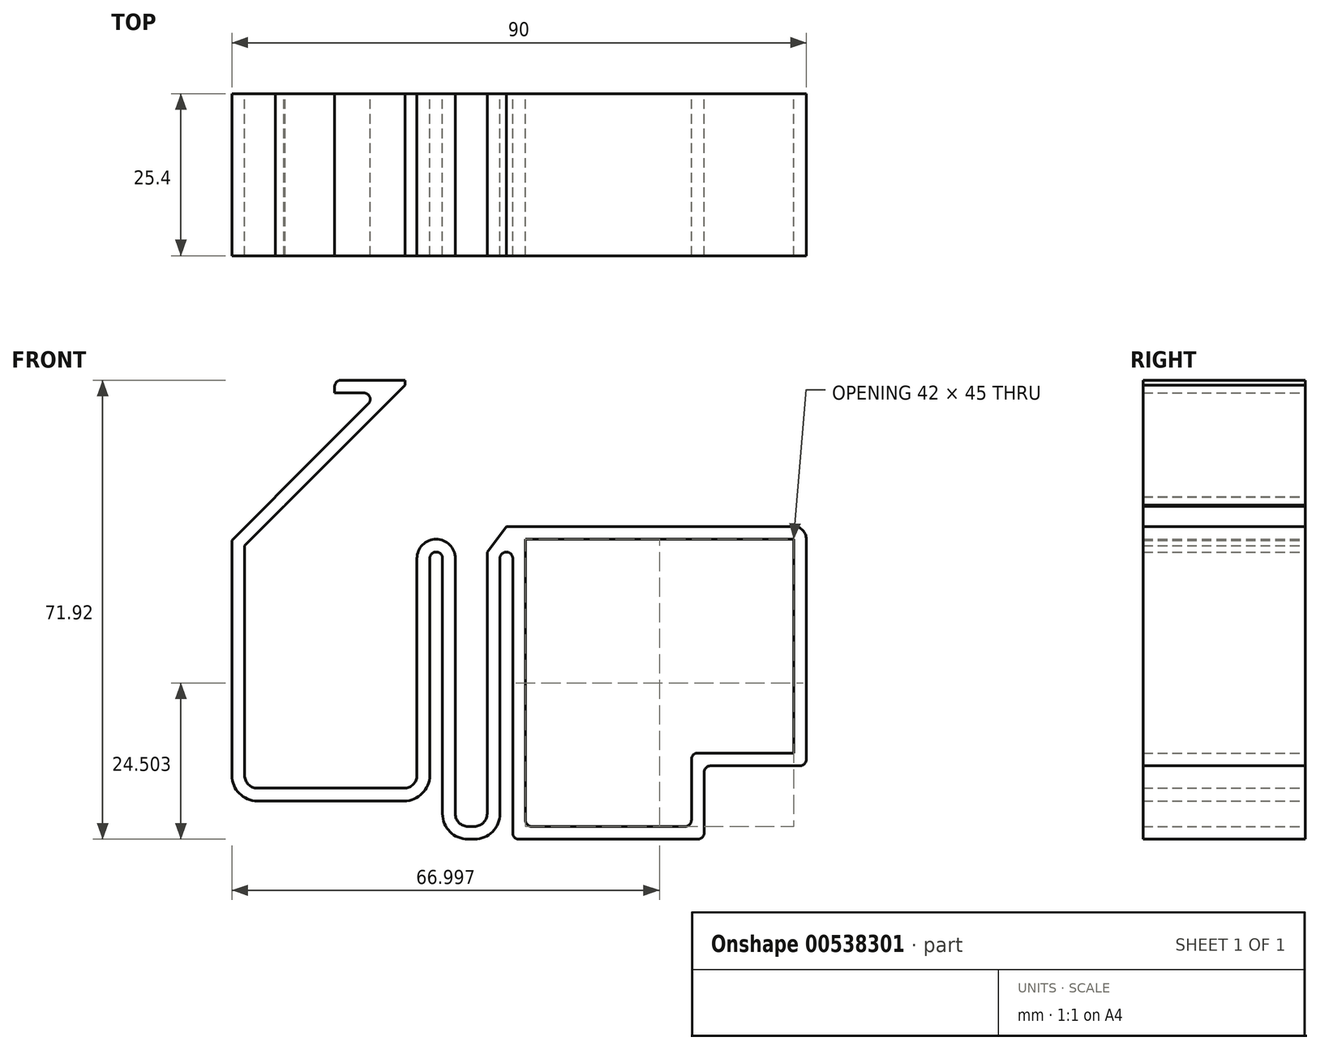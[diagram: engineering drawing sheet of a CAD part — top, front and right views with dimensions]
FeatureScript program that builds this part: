
annotation { "Feature Type Name" : "Feature", "Feature Type Description" : "" }
export const myFeature = defineFeature(function(context is Context, id is Id, definition is map)
    precondition{}
    {
        {
            var Q0;
            Q0=qCreatedBy(makeId("Front.planeOp"),FACE);
            var sketch = newSketch(context, id + "F0", { "sketchPlane" : qUnion([Q0])});
            skLineSegment(sketch, "E0", {"start": v(-44.1, 16.34) * mm, "end": v(-44.1, -17.66) * mm});
            skLineSegment(sketch, "E1", {"start": v(-17.1, -17.66) * mm, "end": v(-17.1, 16.34) * mm});
            skLineSegment(sketch, "E2", {"start": v(-0.1, 16.34) * mm, "end": v(-0.1, -24.66) * mm});
            skLineSegment(sketch, "E3", {"start": v(-11.1, -23.66) * mm, "end": v(-11.1, 16.34) * mm});
            skLineSegment(sketch, "E4", {"start": v(-6.1, -23.66) * mm, "end": v(-6.1, 16.34) * mm});
            skLineSegment(sketch, "E5", {"start": v(-9.1, -25.66) * mm, "end": v(-8.1, -25.66) * mm});
            skArc(sketch, "E6", {"start": v(-11.1, 16.34) * mm, "mid": v(-14.1, 19.34) * mm, "end": v(-17.1, 16.34) * mm});
            skPoint(sketch, "E7.visualSharp", {"position": v(-11.1, -25.66) * mm});
            skArc(sketch, "E7.filletArc", {"start": v(-11.1, -23.66) * mm, "mid": v(-10.5, -25.07) * mm, "end": v(-9.1, -25.66) * mm});
            skPoint(sketch, "E8.visualSharp", {"position": v(-6.1, -25.66) * mm});
            skArc(sketch, "E8.filletArc", {"start": v(-8.1, -25.66) * mm, "mid": v(-6.68, -25.07) * mm, "end": v(-6.1, -23.66) * mm});
            skPoint(sketch, "E9.visualSharp", {"position": v(5.9, -15.66) * mm});
            skPoint(sketch, "E10.visualSharp", {"position": v(-17.1, -25.66) * mm});
            skPoint(sketch, "E11.visualSharp", {"position": v(-44.1, -25.66) * mm});
            skPoint(sketch, "E12.end.orphan", {"position": v(20.34, -15.66) * mm});
            skLineSegment(sketch, "E13", {"start": v(20.34, -15.66) * mm, "end": v(20.9, -15.66) * mm});
            skPoint(sketch, "E14.endSnap0", {"position": v(-3.1, 19.34) * mm});
            skLineSegment(sketch, "E15", {"start": v(-42.1, -19.66) * mm, "end": v(-19.1, -19.66) * mm});
            skPoint(sketch, "E16.visualSharp", {"position": v(-44.1, -19.66) * mm});
            skArc(sketch, "E16.filletArc", {"start": v(-44.1, -17.66) * mm, "mid": v(-43.5, -19.07) * mm, "end": v(-42.1, -19.66) * mm});
            skPoint(sketch, "E17.visualSharp", {"position": v(-17.1, -19.66) * mm});
            skArc(sketch, "E17.filletArc", {"start": v(-19.1, -19.66) * mm, "mid": v(-17.68, -19.07) * mm, "end": v(-17.1, -17.66) * mm});
            skLineSegment(sketch, "E18.0", {"start": v(-2.1, 16.34) * mm, "end": v(-2.1, -25.66) * mm});
            skLineSegment(sketch, "E19.0", {"start": v(-4.1, -23.66) * mm, "end": v(-4.1, 16.34) * mm});
            skLineSegment(sketch, "E19.1", {"start": v(-13.1, -23.66) * mm, "end": v(-13.1, 16.34) * mm});
            skArc(sketch, "E19.2", {"start": v(-13.1, -23.66) * mm, "mid": v(-11.92, -26.49) * mm, "end": v(-9.1, -27.66) * mm});
            skLineSegment(sketch, "E19.3", {"start": v(-9.1, -27.66) * mm, "end": v(-8.1, -27.66) * mm});
            skArc(sketch, "E19.4", {"start": v(-8.1, -27.66) * mm, "mid": v(-5.26, -26.49) * mm, "end": v(-4.1, -23.66) * mm});
            skArc(sketch, "E20", {"start": v(-2.1, 16.34) * mm, "mid": v(-3.1, 17.34) * mm, "end": v(-4.1, 16.34) * mm});
            skLineSegment(sketch, "E21.0", {"start": v(-15.1, -17.66) * mm, "end": v(-15.1, 16.34) * mm});
            skLineSegment(sketch, "E21.1", {"start": v(-46.1, 16.34) * mm, "end": v(-46.1, -17.66) * mm});
            skArc(sketch, "E21.2", {"start": v(-46.1, -17.66) * mm, "mid": v(-44.92, -20.49) * mm, "end": v(-42.1, -21.66) * mm});
            skLineSegment(sketch, "E21.3", {"start": v(-42.1, -21.66) * mm, "end": v(-19.1, -21.66) * mm});
            skArc(sketch, "E21.4", {"start": v(-19.1, -21.66) * mm, "mid": v(-16.26, -20.49) * mm, "end": v(-15.1, -17.66) * mm});
            skArc(sketch, "E22", {"start": v(-13.1, 16.34) * mm, "mid": v(-14.1, 17.34) * mm, "end": v(-15.1, 16.34) * mm});
            skPoint(sketch, "E23.visualSharp", {"position": v(22.9, -15.66) * mm});
            skPoint(sketch, "E24.visualSharp", {"position": v(24.9, -17.66) * mm});
            skLineSegment(sketch, "E25", {"start": v(-9.1, -25.66) * mm, "end": v(-8.1, -25.66) * mm, "construction": true});
            skLineSegment(sketch, "E26", {"start": v(-1.1, -27.66) * mm, "end": v(26.9, -27.66) * mm, "construction": true});
            skLineSegment(sketch, "E27", {"start": v(0.9, -25.66) * mm, "end": v(24.9, -25.66) * mm});
            skPoint(sketch, "E27.endSnap0", {"position": v(15.4, -25.66) * mm});
            skLineSegment(sketch, "E28", {"start": v(-2.1, -25.66) * mm, "end": v(-2.1, -26.66) * mm});
            skLineSegment(sketch, "E29", {"start": v(-2.1, -27.66) * mm, "end": v(27.9, -27.66) * mm});
            skLineSegment(sketch, "E30.trimOffspring", {"start": v(2.9, -25.66) * mm, "end": v(24.9, -25.66) * mm, "construction": true});
            skPoint(sketch, "E31.center.orphan", {"position": v(2.9, -25.66) * mm});
            skPoint(sketch, "E32.start.orphan", {"position": v(5.9, -25.66) * mm});
            skPoint(sketch, "E33.end.orphan", {"position": v(22.9, 19.34) * mm});
            skPoint(sketch, "E34.orphan", {"position": v(-2.1, -36.17) * mm});
            skLineSegment(sketch, "E35", {"start": v(25.9, -15.16) * mm, "end": v(25.9, -24.66) * mm});
            skPoint(sketch, "E36.orphan", {"position": v(39.89, -25.66) * mm});
            skLineSegment(sketch, "E37.0", {"start": v(27.9, -17.16) * mm, "end": v(27.9, -25.66) * mm});
            skLineSegment(sketch, "E38.trimOffspring", {"start": v(39.89, -25.66) * mm, "end": v(45.22, -25.66) * mm});
            skLineSegment(sketch, "E39", {"start": v(27.9, -25.66) * mm, "end": v(27.9, -26.66) * mm});
            skPoint(sketch, "E40.visualSharp", {"position": v(-0.1, -25.66) * mm});
            skArc(sketch, "E40.filletArc", {"start": v(-0.1, -24.66) * mm, "mid": v(0.2, -25.36) * mm, "end": v(0.9, -25.66) * mm});
            skPoint(sketch, "E41.visualSharp", {"position": v(25.9, -25.66) * mm});
            skArc(sketch, "E41.filletArc", {"start": v(24.9, -25.66) * mm, "mid": v(25.61, -25.36) * mm, "end": v(25.9, -24.66) * mm});
            skPoint(sketch, "E42.visualSharp", {"position": v(27.9, -27.66) * mm});
            skArc(sketch, "E42.filletArc", {"start": v(26.9, -27.66) * mm, "mid": v(27.61, -27.36) * mm, "end": v(27.9, -26.66) * mm});
            skPoint(sketch, "E43.visualSharp", {"position": v(-2.1, -27.66) * mm});
            skArc(sketch, "E43.filletArc", {"start": v(-2.1, -26.66) * mm, "mid": v(-1.8, -27.36) * mm, "end": v(-1.1, -27.66) * mm});
            skPoint(sketch, "E44.visualSharp", {"position": v(25.9, -14.16) * mm});
            skArc(sketch, "E44.filletArc", {"start": v(26.9, -14.16) * mm, "mid": v(26.2, -14.45) * mm, "end": v(25.9, -15.16) * mm});
            skPoint(sketch, "E45.visualSharp", {"position": v(27.9, -16.16) * mm});
            skArc(sketch, "E45.filletArc", {"start": v(28.9, -16.16) * mm, "mid": v(28.2, -16.45) * mm, "end": v(27.9, -17.16) * mm});
            skLineSegment(sketch, "E46", {"start": v(41.9, -8.41) * mm, "end": v(41.9, -14.16) * mm});
            skLineSegment(sketch, "E47", {"start": v(36.16, -19.88) * mm, "end": v(36.37, -19.88) * mm});
            skLineSegment(sketch, "E48", {"start": v(26.9, -14.16) * mm, "end": v(41.9, -14.16) * mm});
            skLineSegment(sketch, "E49", {"start": v(41.9, -14.16) * mm, "end": v(41.9, 15.92) * mm});
            skLineSegment(sketch, "E50.0", {"start": v(43.9, -14.16) * mm, "end": v(43.9, 15.92) * mm});
            skLineSegment(sketch, "E51", {"start": v(43.9, -14.16) * mm, "end": v(43.9, -15.14) * mm});
            skLineSegment(sketch, "E52.trimOffspring", {"start": v(28.9, -16.16) * mm, "end": v(42.9, -16.16) * mm});
            skPoint(sketch, "E53.endSnap0", {"position": v(-3.1, 17.34) * mm});
            skPoint(sketch, "E54.orphan", {"position": v(43.83, 17.34) * mm});
            skPoint(sketch, "E55.visualSharp", {"position": v(43.06, 19.34) * mm});
            skPoint(sketch, "E56.visualSharp", {"position": v(43.9, -16.16) * mm});
            skArc(sketch, "E56.filletArc", {"start": v(42.9, -16.16) * mm, "mid": v(43.61, -15.86) * mm, "end": v(43.9, -15.14) * mm});
            skPoint(sketch, "E57.visualSharp", {"position": v(-0.1, 17.34) * mm});
            skLineSegment(sketch, "E58", {"start": v(-44.1, 16.34) * mm, "end": v(-44.1, 18.34) * mm});
            skLineSegment(sketch, "E59", {"start": v(-46.1, 16.34) * mm, "end": v(-46.1, 18.34) * mm});
            skLineSegment(sketch, "E60", {"start": v(-44.1, 18.34) * mm, "end": v(-37.77, 24.66) * mm});
            skLineSegment(sketch, "E61.0", {"start": v(-45.53, 19.73) * mm, "end": v(-39.26, 26) * mm});
            skLineSegment(sketch, "E62", {"start": v(-45.53, 19.73) * mm, "end": v(-46.1, 19.17) * mm});
            skLineSegment(sketch, "E63", {"start": v(-46.1, 18.34) * mm, "end": v(-46.1, 19.17) * mm});
            skArc(sketch, "E64", {"start": v(-37.96, 24.47) * mm, "mid": v(-37.86, 24.56) * mm, "end": v(-37.77, 24.66) * mm});
            skLineSegment(sketch, "E65", {"start": v(-0.04, 18.34) * mm, "end": v(0.08, 18.34) * mm});
            skPoint(sketch, "E66.visualSharp", {"position": v(-0.1, 18.34) * mm});
            skArc(sketch, "E66.filletArc", {"start": v(-0.04, 18.34) * mm, "mid": v(-0.08, 18.33) * mm, "end": v(-0.1, 18.29) * mm});
            skLineSegment(sketch, "E67", {"start": v(-6.1, 14.52) * mm, "end": v(-6.1, 17.34) * mm});
            skLineSegment(sketch, "E68", {"start": v(41.9, 15.92) * mm, "end": v(41.9, 18.34) * mm});
            skPoint(sketch, "E69.visualSharp", {"position": v(43.9, 20.34) * mm});
            skArc(sketch, "E70.trimOffspring", {"start": v(-39.26, 26) * mm, "mid": v(-39.28, 25.98) * mm, "end": v(-39.3, 25.96) * mm});
            skLineSegment(sketch, "E71", {"start": v(-45.53, 19.73) * mm, "end": v(-33.85, 31.42) * mm});
            skLineSegment(sketch, "E72", {"start": v(-44.1, 18.34) * mm, "end": v(-32.43, 30) * mm});
            skLineSegment(sketch, "E73.0", {"start": v(-3.1, 21.34) * mm, "end": v(42.04, 21.34) * mm});
            skLineSegment(sketch, "E74.0", {"start": v(0.08, 19.34) * mm, "end": v(41.9, 19.34) * mm});
            skLineSegment(sketch, "E75", {"start": v(-6.1, 17.34) * mm, "end": v(-3.1, 21.34) * mm});
            skLineSegment(sketch, "E76", {"start": v(-0.1, 16.34) * mm, "end": v(-0.1, 19.34) * mm});
            skLineSegment(sketch, "E77", {"start": v(-0.1, 19.34) * mm, "end": v(0.08, 19.34) * mm});
            skLineSegment(sketch, "E78", {"start": v(43.9, 6.58) * mm, "end": v(43.9, 19.34) * mm});
            skLineSegment(sketch, "E79", {"start": v(36.2, 21.34) * mm, "end": v(41.9, 21.34) * mm});
            skLineSegment(sketch, "E80", {"start": v(41.9, 18.34) * mm, "end": v(41.9, 19.34) * mm});
            skPoint(sketch, "E81.visualSharp", {"position": v(43.9, 21.34) * mm});
            skArc(sketch, "E81.filletArc", {"start": v(43.9, 19.34) * mm, "mid": v(43.32, 20.76) * mm, "end": v(41.9, 21.34) * mm});
            skLineSegment(sketch, "E82", {"start": v(-33.85, 31.42) * mm, "end": v(-24.7, 40.56) * mm});
            skLineSegment(sketch, "E83", {"start": v(-32.43, 30) * mm, "end": v(-18.98, 43.46) * mm});
            skLineSegment(sketch, "E84", {"start": v(-18.98, 43.46) * mm, "end": v(-18.98, 44.26) * mm});
            skLineSegment(sketch, "E85", {"start": v(-18.98, 44.26) * mm, "end": v(-19.06, 44.26) * mm});
            skLineSegment(sketch, "E86", {"start": v(-18.98, 44.26) * mm, "end": v(-21, 44.26) * mm});
            skPoint(sketch, "E87.orphan", {"position": v(-20.43, 44.83) * mm});
            skLineSegment(sketch, "E88", {"start": v(-18.98, 44.26) * mm, "end": v(-28.99, 44.26) * mm});
            skPoint(sketch, "E88.endSnap0", {"position": v(-19.99, 44.26) * mm});
            skLineSegment(sketch, "E89", {"start": v(-29.99, 43.26) * mm, "end": v(-29.99, 42.26) * mm});
            skLineSegment(sketch, "E90", {"start": v(-29.99, 42.26) * mm, "end": v(-25.42, 42.26) * mm});
            skLineSegment(sketch, "E91", {"start": v(-23, 42.26) * mm, "end": v(-23.32, 42.02) * mm});
            skPoint(sketch, "E92.visualSharp", {"position": v(-29.99, 44.26) * mm});
            skArc(sketch, "E92.filletArc", {"start": v(-28.99, 44.26) * mm, "mid": v(-29.7, 43.97) * mm, "end": v(-29.99, 43.26) * mm});
            skArc(sketch, "E93.filletArc", {"start": v(-24.7, 40.56) * mm, "mid": v(-24.5, 41.65) * mm, "end": v(-25.42, 42.26) * mm});
            skSolve(sketch);
        }
        {
            var Q0;
            Q0 = qSketchRegion(id + "F0", true);
            extrude(context, id + "F1", {"entities" : qUnion([Q0]), "depth" : 25.4 * mm, "offsetDistance" : 25.4 * mm});
        }
    });
